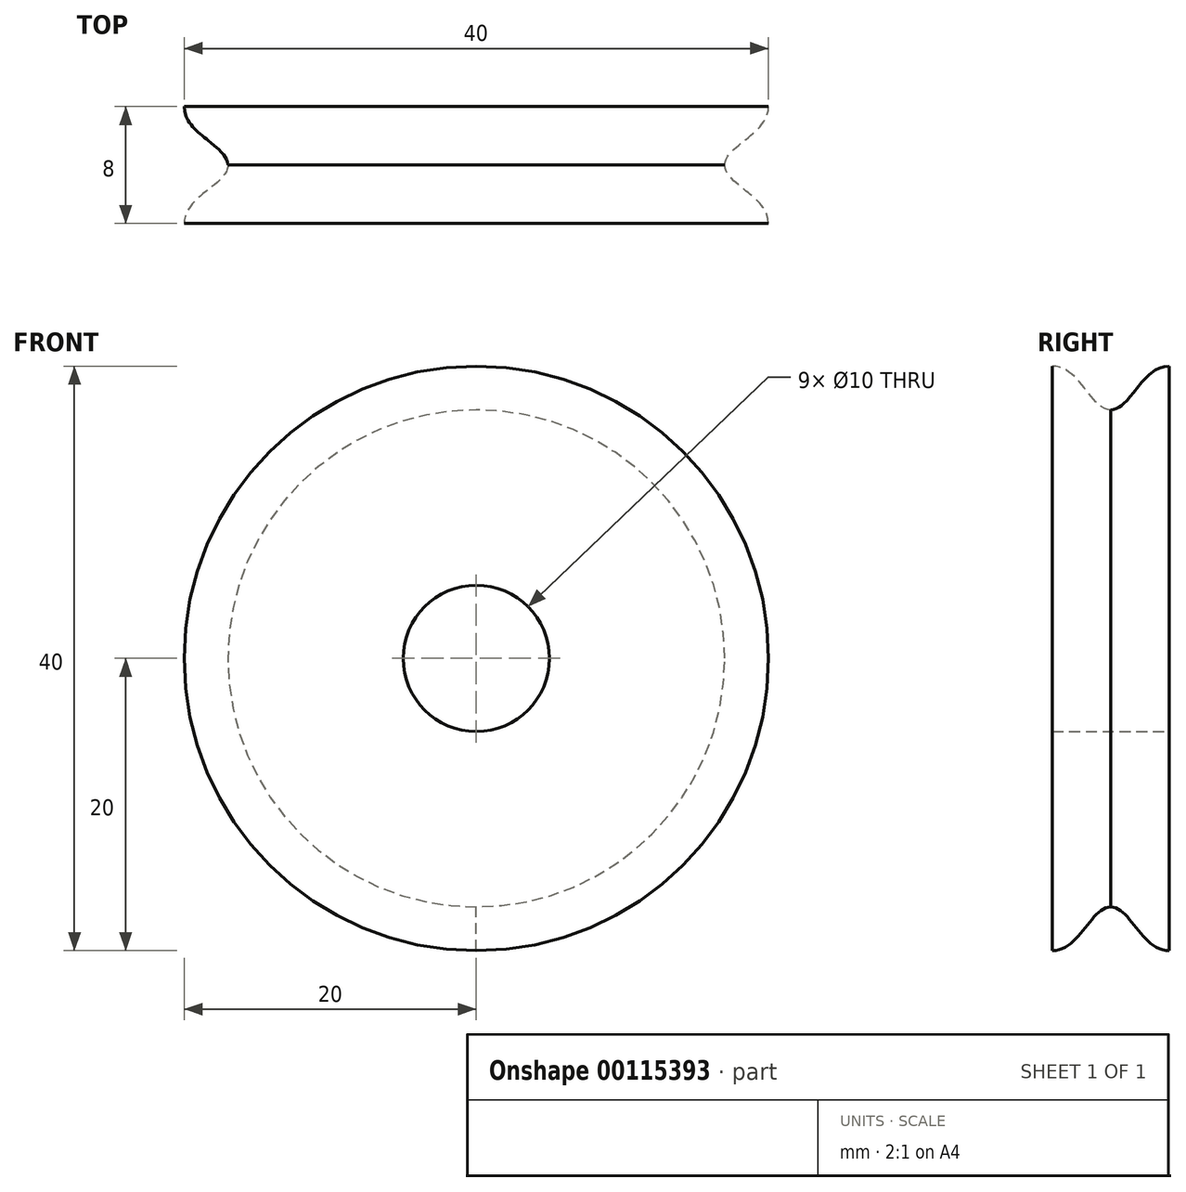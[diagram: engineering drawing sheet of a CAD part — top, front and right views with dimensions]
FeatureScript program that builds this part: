
annotation { "Feature Type Name" : "Feature", "Feature Type Description" : "" }
export const myFeature = defineFeature(function(context is Context, id is Id, definition is map)
    precondition{}
    {
        {
            var Q0;
            Q0=qCreatedBy(makeId("Front.planeOp"),FACE);
            var sketch = newSketch(context, id + "F0", { "sketchPlane" : qUnion([Q0])});
            skCircle(sketch, "E0", {"center": v(0, 0) * mm, "radius": 20 * mm});
            skCircle(sketch, "E1", {"center": v(0, 0) * mm, "radius": 5 * mm});
            skSolve(sketch);
        }
        {
            var Q0;
            Q0 = qSketchRegion(id + "F0", true);
            var Q1;
            Q1=makeQuery(id+"F0.imprint","IMPRINT",FACE,{"disambiguationData":[TD([[makeQuery(id+"F0.imprint","IMPRINT",EDGE,{"derivedFrom":sQuery(id+"F0.wireOp",EDGE,"E0")}),1.0]])]});
            extrude(context, id + "F1", {"entities" : qUnion([Q0, Q1]), "endBound" : BoundingType.SYMMETRIC, "depth" : 8 * mm});
        }
        {
            var Q0;
            Q0=qCreatedBy(makeId("Right.planeOp"),FACE);
            var sketch = newSketch(context, id + "F2", { "sketchPlane" : qUnion([Q0])});
            skLineSegment(sketch, "E2", {"start": v(0, 0) * mm, "end": v(0, 20) * mm});
            skPoint(sketch, "E3", {"position": v(-4, 20) * mm});
            skPoint(sketch, "E4", {"position": v(0, 17) * mm});
            skFitSpline(sketch, "E5", {"points": [v(-4, 20) * mm, v(0, 17) * mm], "startDerivative": vector(5.58, -0.01) * mm, "endDerivative": vector(4.1, -0.14) * mm});
            skFitSpline(sketch, "E6.MirrorCS", {"points": [v(4, 20) * mm, v(0, 17) * mm], "startDerivative": vector(-5.58, -0.01) * mm, "endDerivative": vector(-4.1, -0.14) * mm});
            skLineSegment(sketch, "E7", {"start": v(-4, 20) * mm, "end": v(4, 20) * mm});
            skLineSegment(sketch, "E8", {"start": v(0, 0) * mm, "end": v(-15.51, 0) * mm});
            skSolve(sketch);
        }
        {
            var Q0;
            Q0 = qSketchRegion(id + "F2", true);
            var Q1;
            Q1=sQuery(id+"F2.wireOp",EDGE,"E8");
            revolve(context, id + "F3", {"operationType" : NewBodyOperationType.REMOVE, "entities" : qUnion([Q0]), "axis" : qUnion([Q1]), "revolveType" : RevolveType.FULL, "oppositeDirection" : true});
        }
    });
